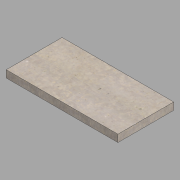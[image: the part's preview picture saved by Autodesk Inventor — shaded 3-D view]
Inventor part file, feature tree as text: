
AUTODESK INVENTOR PART (.ipt)
format: ipt  version: 2022 (Build 260153000, 153)  size: 115,200 bytes
history: native  units: in
note: dims shown in document units (in); Inventor stores cm internally (conversion verified against a paired STEP export)
features: other x1, extrude x1, sketch x1
ambient origin geometry x8: Origin, YZ Plane, XZ Plane, XY Plane, X Axis, Y Axis, Z Axis, Center Point
bodies: Body1 (feature_tree)
feature tree (3):
  other  "Type 1 paver vehicular"
  extrude  "Extrusion1"  Depth=24.0in
  sketch  "Sketch1"  dims[d0=48.0in d1=24.0in d2=3.125in d3=0.0in]
